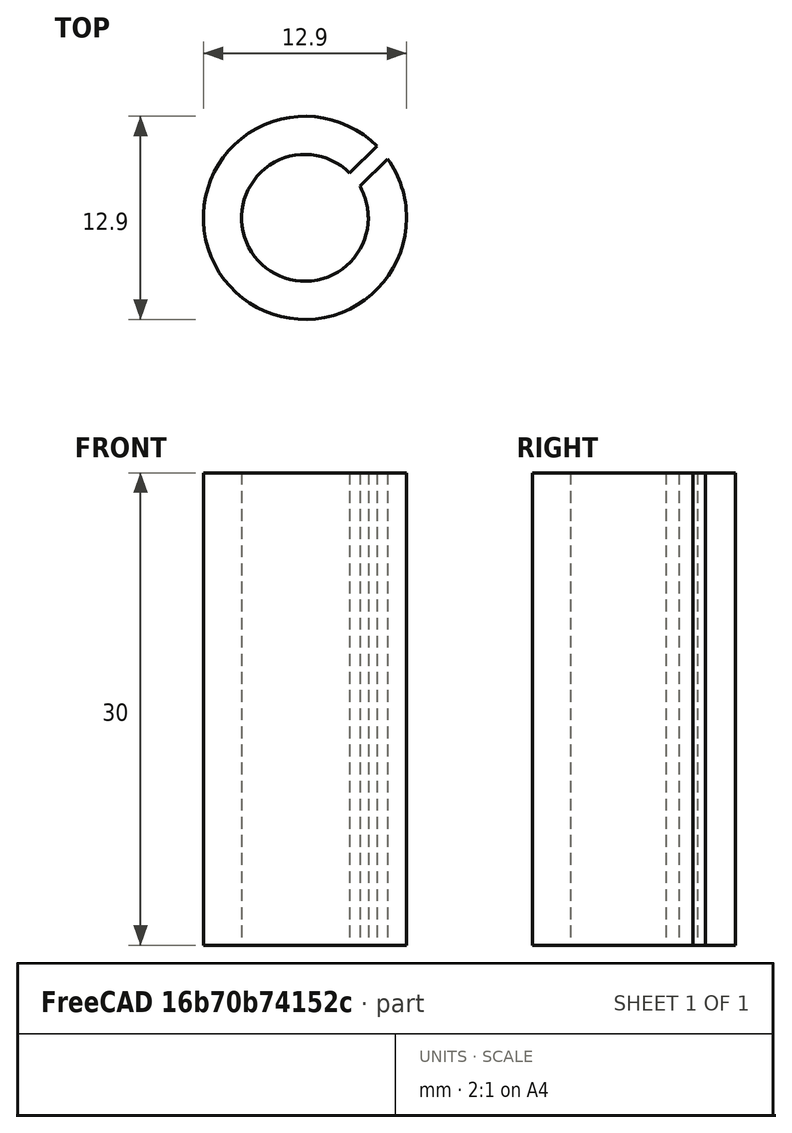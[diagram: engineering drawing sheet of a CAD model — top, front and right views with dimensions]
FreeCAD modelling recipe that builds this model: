
FCSTD DOCUMENT  (FreeCAD 1.1R42891 (Git))
Label: Connector-8mm
License: All rights reserved
LicenseURL: https://en.wikipedia.org/wiki/All_rights_reserved
objects: PartDesign::Body×2, App::Point×2, Sketcher::SketchObject×2, PartDesign::Pad×1, PartDesign::Pocket×1
note: 12 computed .brp shape members not serialized (recipe doc carries the construction recipe); baked Part::Feature solids carry a one-line shape summary decoded from their .brp

FEATURE [PartDesign::Body] Body
  AllowCompound = false
  Origin = -> Origin
FEATURE [App::Point] Origin001
  Role = Origin
FEATURE [App::Point] Origin003
  Role = Origin
FEATURE [Sketcher::SketchObject] Sketch
  ArcFitTolerance = 1e-06
  AttachmentSupport = -> [Origin002]
  ExternalTypes = [0]
  FullyConstrained = false
  MakeInternals = false
  MapMode = 5
  sketch-geometry (2):
    g0: Circle CenterX=-0.092284 CenterY=0 CenterZ=0 NormalX=0 NormalY=0 NormalZ=1 AngleXU=0 Radius=4.025
    g1: Circle CenterX=-0.092284 CenterY=0 CenterZ=0 NormalX=0 NormalY=0 NormalZ=1 AngleXU=0 Radius=6.45
  constraints (4):
    c: PointOnObject(g0,g-1)
    c: Coincident(g1,g0)
    c: Diameter(g0) = 8.05
    c: Diameter(g1) = 12.9
FEATURE [PartDesign::Pad] Pad
  Direction = (0,0,1)
  Length = 30
  Length2 = 10
  Profile = -> Sketch
  ReferenceAxis = -> Sketch [N_Axis]
  Refine = true
  Suppressed = false
  Type = 0
FEATURE [Sketcher::SketchObject] Sketch001
  ArcFitTolerance = 1e-06
  AttachmentSupport = -> [Pad]
  ExternalTypes = [0]
  FullyConstrained = false
  MakeInternals = false
  MapMode = 5
  Placement = pos=(0,0,30) rot=(0,0,1;0rad)
  sketch-geometry (4):
    g0: LineSegment StartX=5.73373 StartY=4.29018 StartZ=0 EndX=5.00053 EndY=5.04375 EndZ=0
    g1: LineSegment StartX=5.00053 StartY=5.04375 StartZ=0 EndX=1.95484 EndY=2.08039 EndZ=0
    g2: LineSegment StartX=1.95484 StartY=2.08039 StartZ=0 EndX=2.68805 EndY=1.32681 EndZ=0
    g3: LineSegment StartX=2.68805 StartY=1.32681 StartZ=0 EndX=5.73373 EndY=4.29018 EndZ=0
  constraints (4):
    c: Coincident(g0,g1)
    c: Coincident(g1,g2)
    c: Coincident(g2,g3)
    c: Coincident(g3,g0)
FEATURE [PartDesign::Pocket] Pocket
  BaseFeature = -> Pad
  Direction = (0,0,-1)
  Length = 30
  Length2 = 5
  Profile = -> Sketch001
  ReferenceAxis = -> Sketch001 [N_Axis]
  Refine = true
  Suppressed = false
  Type = 0
FEATURE [PartDesign::Body] Body001
  AllowCompound = false
  Group = -> [Sketch,Pad,Sketch001,Pocket]
  Origin = -> Origin002
  Tip = -> Pocket
